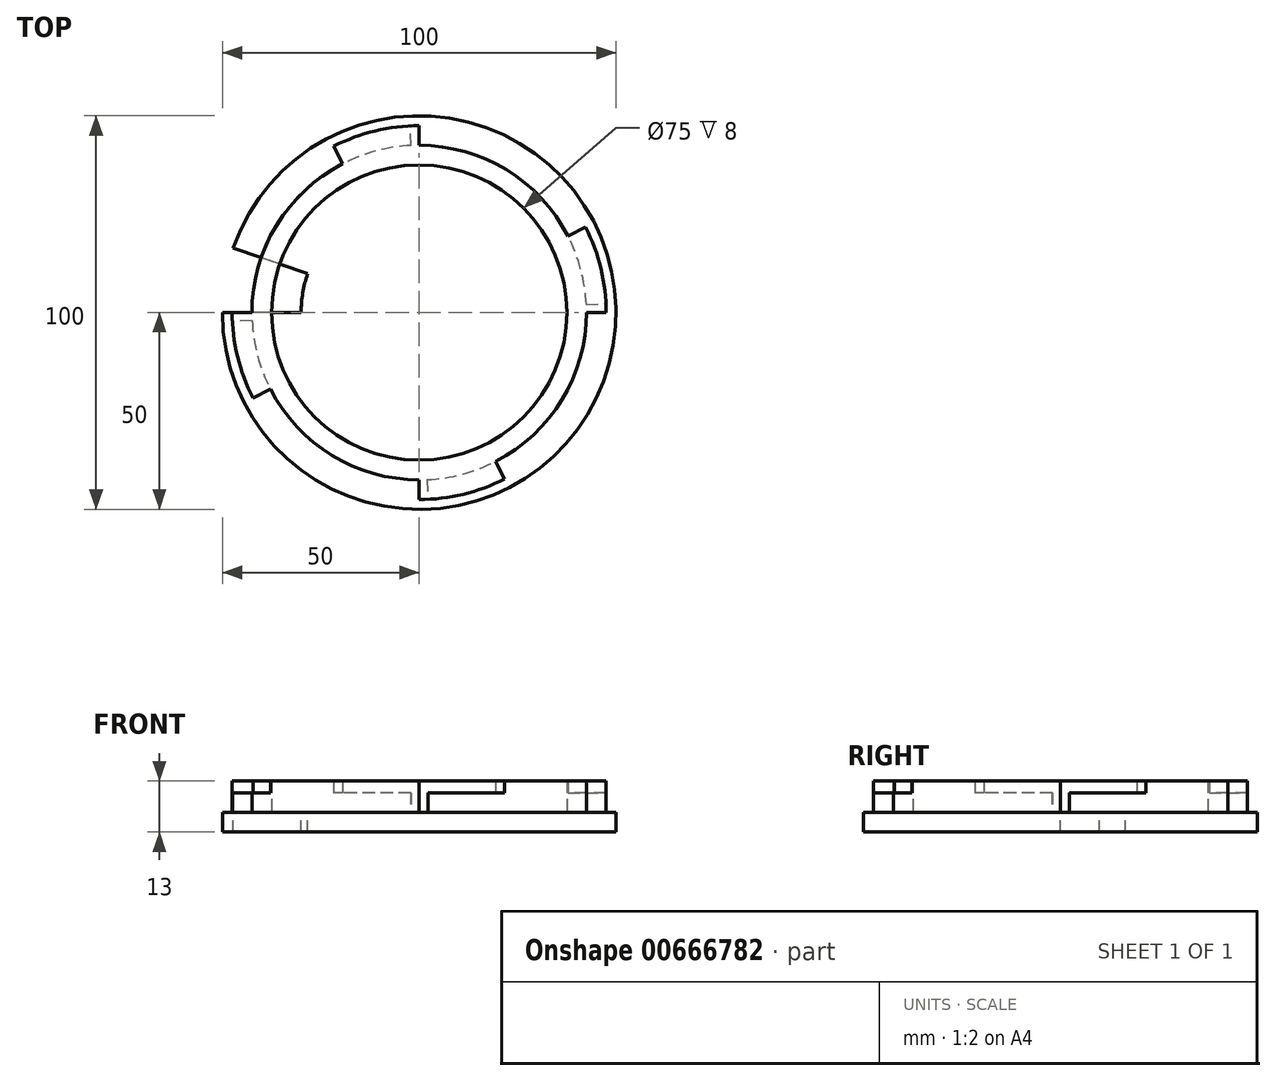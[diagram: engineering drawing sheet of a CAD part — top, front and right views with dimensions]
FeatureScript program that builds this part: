
annotation { "Feature Type Name" : "Feature", "Feature Type Description" : "" }
export const myFeature = defineFeature(function(context is Context, id is Id, definition is map)
    precondition{}
    {
        {
            var Q0;
            Q0=qCreatedBy(makeId("Top.planeOp"),FACE);
            var sketch = newSketch(context, id + "F0", { "sketchPlane" : qUnion([Q0])});
            skCircle(sketch, "E0", {"center": v(0, 0) * mm, "radius": 50 * mm});
            skCircle(sketch, "E1", {"center": v(0, 0) * mm, "radius": 47.5 * mm});
            skLineSegment(sketch, "E2", {"start": v(0, 42.5) * mm, "end": v(0, 47.5) * mm});
            skArc(sketch, "E3", {"start": v(0, 42.5) * mm, "mid": v(-10, 41.3) * mm, "end": v(-19.44, 37.8) * mm});
            skLineSegment(sketch, "E4", {"start": v(-19.44, 37.8) * mm, "end": v(-21.73, 42.24) * mm});
            skLineSegment(sketch, "E5", {"start": v(-2, 42.45) * mm, "end": v(-2.24, 47.45) * mm});
            skLineSegment(sketch, "E6.1.0", {"start": v(-37.8, -19.44) * mm, "end": v(-42.24, -21.73) * mm});
            skArc(sketch, "E6.1.1", {"start": v(-42.5, 0) * mm, "mid": v(-41.3, -10) * mm, "end": v(-37.8, -19.44) * mm});
            skLineSegment(sketch, "E6.1.2", {"start": v(-42.5, 0) * mm, "end": v(-47.5, 0) * mm});
            skLineSegment(sketch, "E6.1.3", {"start": v(-42.45, -2) * mm, "end": v(-47.45, -2.24) * mm});
            skLineSegment(sketch, "E6.2.0", {"start": v(19.44, -37.8) * mm, "end": v(21.73, -42.24) * mm});
            skArc(sketch, "E6.2.1", {"start": v(0, -42.5) * mm, "mid": v(10, -41.3) * mm, "end": v(19.44, -37.8) * mm});
            skLineSegment(sketch, "E6.2.2", {"start": v(0, -42.5) * mm, "end": v(0, -47.5) * mm});
            skLineSegment(sketch, "E6.2.3", {"start": v(2, -42.45) * mm, "end": v(2.24, -47.45) * mm});
            skLineSegment(sketch, "E6.3.0", {"start": v(37.8, 19.44) * mm, "end": v(42.24, 21.73) * mm});
            skArc(sketch, "E6.3.1", {"start": v(42.5, 0) * mm, "mid": v(41.3, 10) * mm, "end": v(37.8, 19.44) * mm});
            skLineSegment(sketch, "E6.3.2", {"start": v(42.5, 0) * mm, "end": v(47.5, 0) * mm});
            skLineSegment(sketch, "E6.3.3", {"start": v(42.45, 2) * mm, "end": v(47.45, 2.24) * mm});
            skCircle(sketch, "E7", {"center": v(0, 0) * mm, "radius": 42.5 * mm});
            skLineSegment(sketch, "E8", {"start": v(-37.8, -19.44) * mm, "end": v(-33.35, -17.15) * mm});
            skCircle(sketch, "E9", {"center": v(0, 0) * mm, "radius": 37.5 * mm});
            skSolve(sketch);
        }
        {
            var Q0;
            Q0=makeQuery(id+"F0.imprint","IMPRINT",FACE,{"disambiguationData":[TD([[makeQuery(id+"F0.imprint","IMPRINT",EDGE,{"derivedFrom":sQuery(id+"F0.wireOp",EDGE,"E9")}),-1.0]])]});
            extrude(context, id + "F1", {"entities" : qUnion([Q0]), "depth" : 8 * mm, "offsetDistance" : 25 * mm});
        }
        {
            var Q0;
            {var subQ0=sQuery(id+"F0.wireOp",EDGE,"E6.1.2");Q0=makeQuery(id+"F0.imprint","IMPRINT",FACE,{"disambiguationData":[TD([[makeQuery(id+"F0.imprint","IMPRINT",EDGE,{"derivedFrom":subQ0}),1.0]])]});}
            var Q1;
            {var subQ0=sQuery(id+"F0.wireOp",EDGE,"E2");Q1=makeQuery(id+"F0.imprint","IMPRINT",FACE,{"disambiguationData":[TD([[makeQuery(id+"F0.imprint","IMPRINT",EDGE,{"derivedFrom":subQ0}),1.0]])]});}
            var Q2;
            {var subQ0=sQuery(id+"F0.wireOp",EDGE,"E6.3.2");Q2=makeQuery(id+"F0.imprint","IMPRINT",FACE,{"disambiguationData":[TD([[makeQuery(id+"F0.imprint","IMPRINT",EDGE,{"derivedFrom":subQ0}),1.0]])]});}
            var Q3;
            {var subQ0=sQuery(id+"F0.wireOp",EDGE,"E6.2.2");Q3=makeQuery(id+"F0.imprint","IMPRINT",FACE,{"disambiguationData":[TD([[makeQuery(id+"F0.imprint","IMPRINT",EDGE,{"derivedFrom":subQ0}),1.0]])]});}
            extrude(context, id + "F2", {"entities" : qUnion([Q0, Q1, Q2, Q3]), "operationType" : NewBodyOperationType.ADD, "depth" : 8 * mm, "offsetDistance" : 25 * mm});
        }
        {
            var Q0;
            {var subQ0=sQuery(id+"F0.wireOp",EDGE,"E6.1.0");Q0=makeQuery(id+"F0.imprint","IMPRINT",FACE,{"disambiguationData":[TD([[makeQuery(id+"F0.imprint","IMPRINT",EDGE,{"derivedFrom":subQ0}),-1.0]])]});}
            var Q1;
            {var subQ0=sQuery(id+"F0.wireOp",EDGE,"E6.2.0");Q1=makeQuery(id+"F0.imprint","IMPRINT",FACE,{"disambiguationData":[TD([[makeQuery(id+"F0.imprint","IMPRINT",EDGE,{"derivedFrom":subQ0}),-1.0]])]});}
            var Q2;
            {var subQ0=sQuery(id+"F0.wireOp",EDGE,"E6.3.0");Q2=makeQuery(id+"F0.imprint","IMPRINT",FACE,{"disambiguationData":[TD([[makeQuery(id+"F0.imprint","IMPRINT",EDGE,{"derivedFrom":subQ0}),-1.0]])]});}
            var Q3;
            {var subQ0=sQuery(id+"F0.wireOp",EDGE,"E4");Q3=makeQuery(id+"F0.imprint","IMPRINT",FACE,{"disambiguationData":[TD([[makeQuery(id+"F0.imprint","IMPRINT",EDGE,{"derivedFrom":subQ0}),-1.0]])]});}
            extrude(context, id + "F3", {"entities" : qUnion([Q0, Q1, Q2, Q3]), "operationType" : NewBodyOperationType.ADD, "depth" : 8 * mm, "offsetDistance" : 25 * mm, "hasSecondDirection" : true, "secondDirectionOppositeDirection" : true, "secondDirectionDepth" : -5 * mm});
        }
        {
            var Q0;
            Q0=qCreatedBy(makeId("Top.planeOp"),FACE);
            var sketch = newSketch(context, id + "F4", { "sketchPlane" : qUnion([Q0])});
            skCircle(sketch, "E10", {"center": v(0, 0) * mm, "radius": 50 * mm});
            skSolve(sketch);
        }
        {
            var Q0;
            Q0=qSketchRegion(id+"F4",true);
            extrude(context, id + "F5", {"entities" : qUnion([Q0]), "operationType" : NewBodyOperationType.ADD, "depth" : -5 * mm, "offsetDistance" : 25 * mm});
        }
        {
            var Q0;
            Q0=qCreatedBy(makeId("Top.planeOp"),FACE);
            var sketch = newSketch(context, id + "F6", { "sketchPlane" : qUnion([Q0])});
            skArc(sketch, "E11", {"start": v(-47.22, 16.43) * mm, "mid": v(-49.3, 8.33) * mm, "end": v(-50, 0) * mm});
            skArc(sketch, "E12", {"start": v(-30, 0) * mm, "mid": v(-29.58, 5) * mm, "end": v(-28.33, 9.86) * mm});
            skLineSegment(sketch, "E13", {"start": v(-28.33, 9.86) * mm, "end": v(-47.22, 16.43) * mm});
            skLineSegment(sketch, "E14", {"start": v(-30, 0) * mm, "end": v(-50, 0) * mm});
            skSolve(sketch);
        }
        {
            var Q0;
            Q0=qSketchRegion(id+"F6",true);
            extrude(context, id + "F7", {"entities" : qUnion([Q0]), "operationType" : NewBodyOperationType.REMOVE, "oppositeDirection" : true, "depth" : 5 * mm, "offsetDistance" : 25 * mm});
        }
    });
